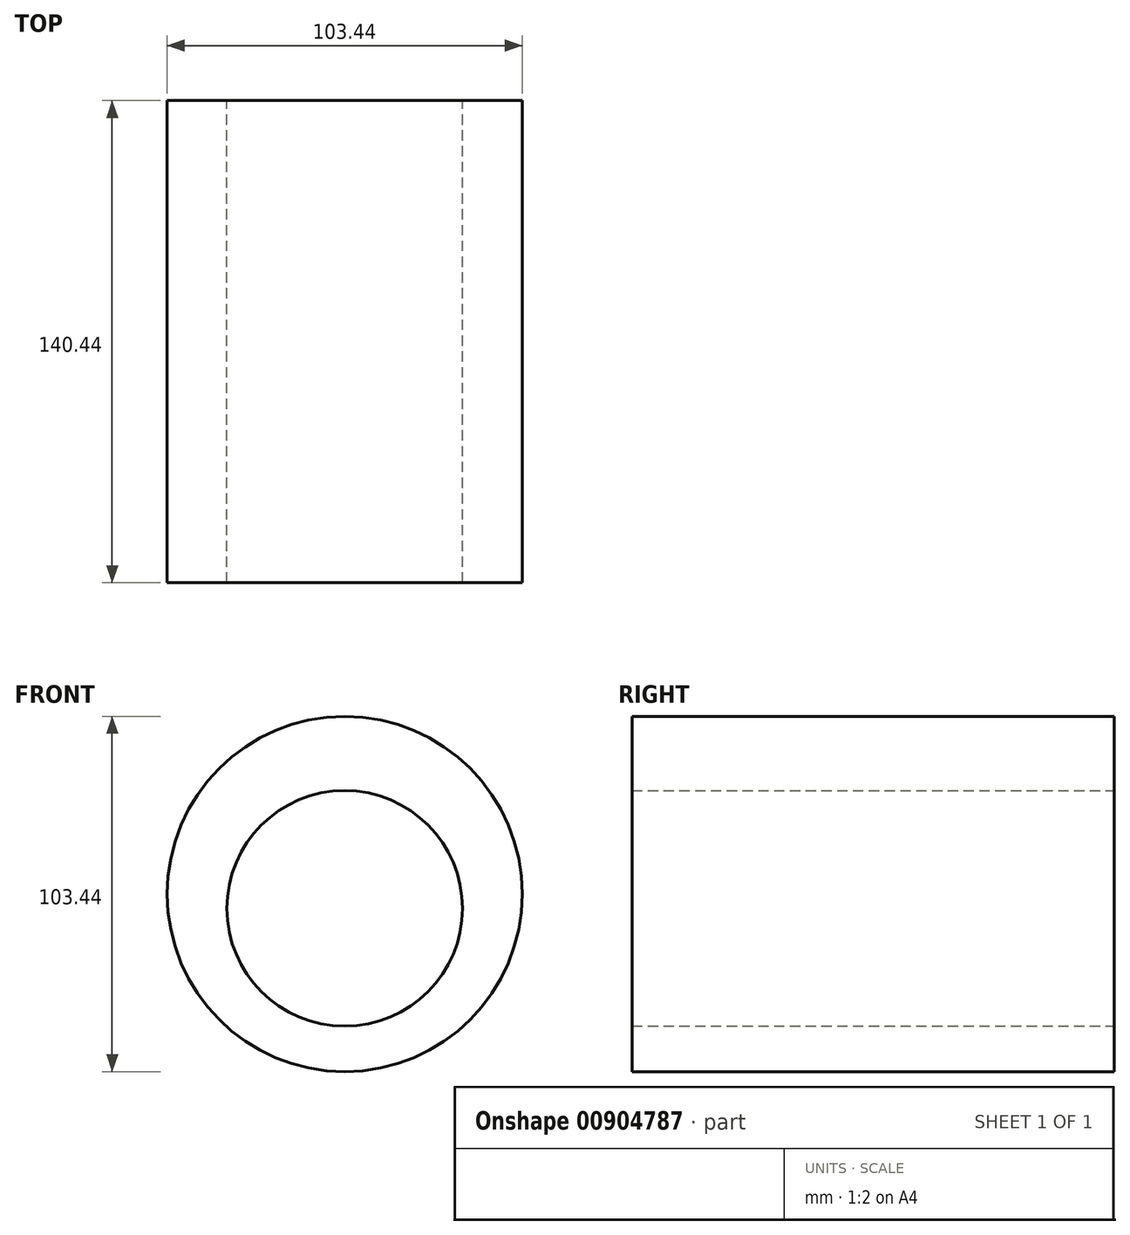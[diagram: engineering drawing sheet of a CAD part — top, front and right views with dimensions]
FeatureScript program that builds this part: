
annotation { "Feature Type Name" : "Feature", "Feature Type Description" : "" }
export const myFeature = defineFeature(function(context is Context, id is Id, definition is map)
    precondition{}
    {
        {
            var Q0;
            Q0=qCreatedBy(makeId("Front.planeOp"),FACE);
            var sketch = newSketch(context, id + "F0", { "sketchPlane" : qUnion([Q0])});
            skFitSpline(sketch, "E0", {"points": [v(0, 0) * mm, v(-22.5, 0) * mm, v(-7.92, 30.22) * mm, v(14.38, 65) * mm, v(15, 121.64) * mm, v(21.88, 155.5) * mm], "startDerivative": vector(-193.93, -39.19) * mm, "endDerivative": vector(49.85, 157) * mm});
            skCircle(sketch, "E1", {"center": v(52.09, 143.39) * mm, "radius": 51.72 * mm});
            skCircle(sketch, "E2", {"center": v(52.09, 139.22) * mm, "radius": 34.32 * mm});
            skSolve(sketch);
        }
        {
            var Q0;
            Q0 = qSketchRegion(id + "F0", true);
            var Q1;
            Q1=sQuery(id+"F0.wireOp",EDGE,"E2");
            extrude(context, id + "F1", {"entities" : qUnion([Q0]), "surfaceEntities" : qUnion([Q1]), "depth" : 140.44 * mm, "offsetDistance" : 25.4 * mm});
        }
    });
